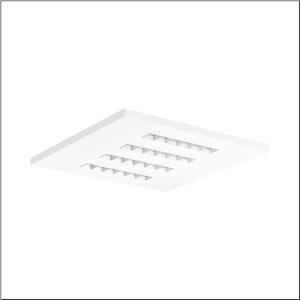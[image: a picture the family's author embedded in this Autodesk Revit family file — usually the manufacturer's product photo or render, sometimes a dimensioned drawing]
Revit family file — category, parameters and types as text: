
# Revit family: silica_r__21_square_51mx6mdu44w_c9d7
name_source: partatom
category: Lighting Fixtures
units: mm (PartAtom-declared; Revit-internal decimal feet)

## family parameters
Cut with Voids When Loaded = No
Host = Face
Light Source = No
Part Type = Normal
Room Calculation Point = No
Round Connector Dimension = Use Diameter
Shared = No

## types (1)
- --- (1 x LED, 4600 lm, 27.2 W, 4000K)
    Apparent Load = 27 VA
    CIE Flux Codes = 83 98 100 100 100
    Color Rendering = 80
    Color Temperature = 4000K
    Default Elevation = 1800 mm
    Description = Silica® 21 Square, office luminaire, primary light control with lens, of PMMA, primary anti-glare with reflector, of PC, white, CAT 2 (L<= 3000cd/m²), light emission: direct distribution, primary light characteristic: symmetric, installation type: lay-in mounting, LED, rated luminous flux: 4.600lm, luminous efficacy: 169lm/W, light colour: 840, colour temperature: 4000K, with terminal, 5-pole, mains connection: 220..240V, AC, 50/60Hz, rated input power: 27.2W, luminaire housing, of sheet steel, coated, traffic white (RAL 9016), module: M625, length: 622mm, width: 622mm, height: 33mm, protection rating (complete): IP20, insulation class (complete): insulation class I (protective earthing), certification: CE, permissible operating ambient temperature: -20..+40°C, standard: EN 50419, packaging unit: 1 piece
    Height = 0 mm  [stored 0 ft]
    Lamp = 1 x LED
    Lamp Light Flux = 4600 lm
    Lamp Power = 27.2 W
    Lamp count = 1
    Length = 622 mm
    Luminous efficacy = 169 lm/W
    Manufacturer = Siteco
    ModVariant = No
    Model = 51MX6MDU44W
    Mounting Place = Ceiling
    Mounting Type = Recessed
    Number of Poles = 1
    OnlyDefault = Yes
    Power Factor = 1
    Product Name = Silica® 21 Square
    Product group = office luminaire | ceiling recessed
    ProductGroupID = 401
    Protection Class = Protection class I
    Protection Degree = IP 20
    RLX_Detail_Level = 1
    RLX_Emergency_Light_Flux = 0 lm
    RLX_Emergency_Type = 0
    RLX_Emergency_Type_DB = No
    RlxData = <blob elided: 18581 chars, md5=2124315e>
    Socket = socket
    Standby Power = 0 W
    System Light Flux = 4600 lm
    System Power = 27 W
    Type Comments = factory setting: luminous flux: 100 % | dim-lin: 254 | 366 mA
    Type Image = l_1275220.jpg
    URL = http://relux.com
    VarID = @adj_036007
    Voltage = 0 V
    Weight = 0.00 kg
    Width = 622 mm

note: [stored X ft] marks values corroborated as IEEE doubles in the binary element streams (Revit-internal decimal feet)

## geometry (parser evidence)
native form markers: Blend x4, Sweep x11
no freeform markers — native parametric forms only
